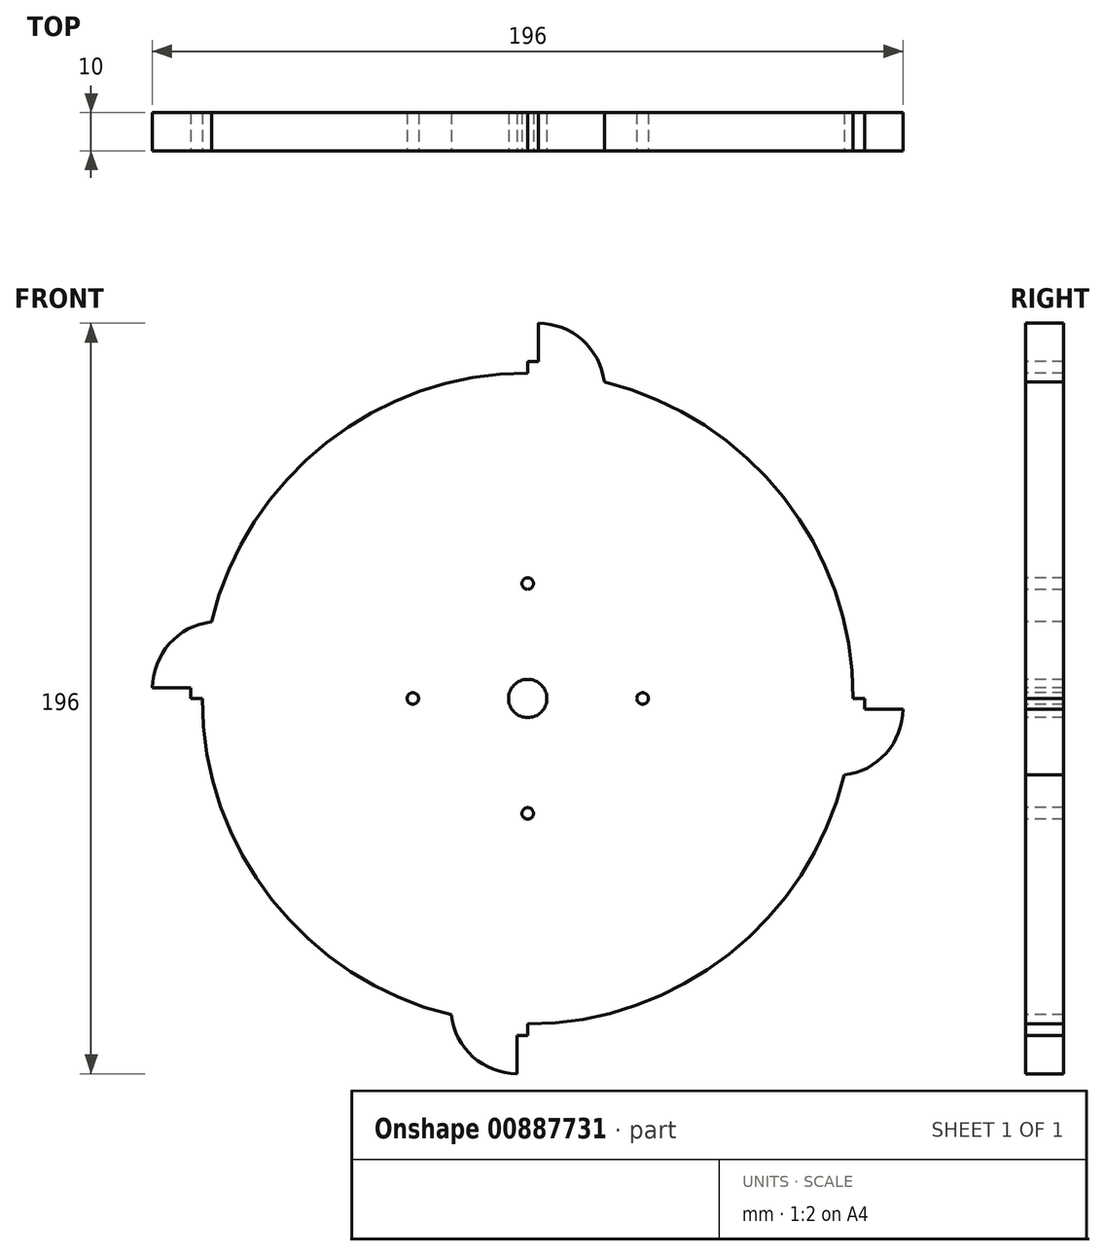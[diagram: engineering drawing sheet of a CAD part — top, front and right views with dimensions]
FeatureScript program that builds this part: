
annotation { "Feature Type Name" : "Feature", "Feature Type Description" : "" }
export const myFeature = defineFeature(function(context is Context, id is Id, definition is map)
    precondition{}
    {
        {
            var Q0;
            Q0=qCreatedBy(makeId("Front.planeOp"),FACE);
            var sketch = newSketch(context, id + "F0", { "sketchPlane" : qUnion([Q0])});
            skCircle(sketch, "E0", {"center": v(0, 0) * mm, "radius": 85 * mm});
            skSolve(sketch);
        }
        {
            var Q0;
            Q0=makeQuery(id+"F0.imprint","IMPRINT",FACE,{"disambiguationData":[TD([[makeQuery(id+"F0.imprint","IMPRINT",EDGE,{"derivedFrom":sQuery(id+"F0.wireOp",EDGE,"E0")}),1.0]])]});
            extrude(context, id + "F1", {"entities" : qUnion([Q0]), "depth" : 10 * mm, "offsetDistance" : 25 * mm});
        }
        {
            var Q0;
            Q0=makeQuery(id+"F1.opExtrude","CAP_FACE",FACE,{"disambiguationData":[OSD([sQuery(id+"F0.wireOp",EDGE,"E0")])],"isStart":false});
            var sketch = newSketch(context, id + "F2", { "sketchPlane" : qUnion([Q0])});
            skLineSegment(sketch, "E1", {"start": v(0, 0) * mm, "end": v(0, 85) * mm});
            skLineSegment(sketch, "E2", {"start": v(0, 85) * mm, "end": v(0, 88) * mm});
            skLineSegment(sketch, "E3", {"start": v(0, 88) * mm, "end": v(2.75, 88) * mm});
            skLineSegment(sketch, "E4", {"start": v(2.75, 88) * mm, "end": v(2.75, 98) * mm});
            skArc(sketch, "E5", {"start": v(20, 82.61) * mm, "mid": v(14.3, 93.6) * mm, "end": v(2.75, 98) * mm});
            skArc(sketch, "E6.1.0", {"start": v(82.61, -20) * mm, "mid": v(93.6, -14.3) * mm, "end": v(98, -2.75) * mm});
            skLineSegment(sketch, "E6.1.1", {"start": v(88, -2.75) * mm, "end": v(98, -2.75) * mm});
            skLineSegment(sketch, "E6.1.2", {"start": v(88, 0) * mm, "end": v(88, -2.75) * mm});
            skLineSegment(sketch, "E6.1.3", {"start": v(85, 0) * mm, "end": v(88, 0) * mm});
            skArc(sketch, "E6.2.0", {"start": v(-20, -82.61) * mm, "mid": v(-14.3, -93.6) * mm, "end": v(-2.75, -98) * mm});
            skLineSegment(sketch, "E6.2.1", {"start": v(-2.75, -88) * mm, "end": v(-2.75, -98) * mm});
            skLineSegment(sketch, "E6.2.2", {"start": v(0, -88) * mm, "end": v(-2.75, -88) * mm});
            skLineSegment(sketch, "E6.2.3", {"start": v(0, -85) * mm, "end": v(0, -88) * mm});
            skArc(sketch, "E6.3.0", {"start": v(-82.61, 20) * mm, "mid": v(-93.6, 14.3) * mm, "end": v(-98, 2.75) * mm});
            skLineSegment(sketch, "E6.3.1", {"start": v(-88, 2.75) * mm, "end": v(-98, 2.75) * mm});
            skLineSegment(sketch, "E6.3.2", {"start": v(-88, 0) * mm, "end": v(-88, 2.75) * mm});
            skLineSegment(sketch, "E6.3.3", {"start": v(-85, 0) * mm, "end": v(-88, 0) * mm});
            skPoint(sketch, "E6.center", {"position": v(0, 0) * mm});
            skLineSegment(sketch, "E6.anchor1", {"start": v(0, 0) * mm, "end": v(0, 85) * mm, "construction": true});
            skLineSegment(sketch, "E6.anchor2", {"start": v(0, 0) * mm, "end": v(-85, 0) * mm, "construction": true});
            skSolve(sketch);
        }
        {
            var Q0;
            Q0 = qSketchRegion(id + "F2", true);
            var Q1;
            {var subQ1=sQuery(id+"F2.wireOp",EDGE,"E2");Q1=makeQuery(id+"F2.imprint","IMPRINT",FACE,{"disambiguationData":[TD([[makeQuery(id+"F2.imprint","IMPRINT",EDGE,{"derivedFrom":subQ1}),-1.0]])]});}
            var Q2;
            {var subQ1=sQuery(id+"F2.wireOp",EDGE,"E6.3.0");Q2=makeQuery(id+"F2.imprint","IMPRINT",FACE,{"disambiguationData":[TD([[makeQuery(id+"F2.imprint","IMPRINT",EDGE,{"derivedFrom":subQ1}),1.0]])]});}
            var Q3;
            {var subQ1=sQuery(id+"F2.wireOp",EDGE,"E6.2.0");Q3=makeQuery(id+"F2.imprint","IMPRINT",FACE,{"disambiguationData":[TD([[makeQuery(id+"F2.imprint","IMPRINT",EDGE,{"derivedFrom":subQ1}),1.0]])]});}
            var Q4;
            {var subQ1=sQuery(id+"F2.wireOp",EDGE,"E6.1.0");Q4=makeQuery(id+"F2.imprint","IMPRINT",FACE,{"disambiguationData":[TD([[makeQuery(id+"F2.imprint","IMPRINT",EDGE,{"derivedFrom":subQ1}),1.0]])]});}
            extrude(context, id + "F3", {"entities" : qUnion([Q0, Q1, Q2, Q3, Q4]), "operationType" : NewBodyOperationType.ADD, "oppositeDirection" : true, "depth" : 10 * mm, "offsetDistance" : 25 * mm});
        }
        {
            var Q0;
            {var subQ0=sQuery(id+"F0.wireOp",EDGE,"E0");Q0=makeQuery(id+"F3.boolean.opBoolean","MERGE",FACE,{"derivedFrom":[makeQuery(id+"F1.opExtrude","CAP_FACE",FACE,{"disambiguationData":[OSD([subQ0])],"isStart":false}),makeQuery(id+"F3.opExtrude","CAP_FACE",FACE,{"disambiguationData":[OSD([subQ0,sQuery(id+"F2.wireOp",EDGE,"E2"),sQuery(id+"F2.wireOp",EDGE,"E3"),sQuery(id+"F2.wireOp",EDGE,"E4"),sQuery(id+"F2.wireOp",EDGE,"E5")])],"isStart":true}),makeQuery(id+"F3.opExtrude","CAP_FACE",FACE,{"disambiguationData":[OSD([subQ0,sQuery(id+"F2.wireOp",EDGE,"E6.1.0"),sQuery(id+"F2.wireOp",EDGE,"E6.1.1"),sQuery(id+"F2.wireOp",EDGE,"E6.1.2"),sQuery(id+"F2.wireOp",EDGE,"E6.1.3")])],"isStart":true}),makeQuery(id+"F3.opExtrude","CAP_FACE",FACE,{"disambiguationData":[OSD([subQ0,sQuery(id+"F2.wireOp",EDGE,"E6.2.0"),sQuery(id+"F2.wireOp",EDGE,"E6.2.1"),sQuery(id+"F2.wireOp",EDGE,"E6.2.2"),sQuery(id+"F2.wireOp",EDGE,"E6.2.3")])],"isStart":true}),makeQuery(id+"F3.opExtrude","CAP_FACE",FACE,{"disambiguationData":[OSD([subQ0,sQuery(id+"F2.wireOp",EDGE,"E6.3.0"),sQuery(id+"F2.wireOp",EDGE,"E6.3.1"),sQuery(id+"F2.wireOp",EDGE,"E6.3.2"),sQuery(id+"F2.wireOp",EDGE,"E6.3.3")])],"isStart":true})]});}
            var sketch = newSketch(context, id + "F4", { "sketchPlane" : qUnion([Q0])});
            skCircle(sketch, "E7", {"center": v(0, 0) * mm, "radius": 5 * mm});
            skCircle(sketch, "E8", {"center": v(0, 30) * mm, "radius": 1.5 * mm});
            skCircle(sketch, "E9.4.0", {"center": v(-30, 0) * mm, "radius": 1.5 * mm});
            skCircle(sketch, "E9.8.0", {"center": v(0, -30) * mm, "radius": 1.5 * mm});
            skCircle(sketch, "E9.12.0", {"center": v(30, 0) * mm, "radius": 1.5 * mm});
            skSolve(sketch);
        }
        {
            var Q0;
            Q0=makeQuery(id+"F4.imprint","IMPRINT",FACE,{"disambiguationData":[TD([[makeQuery(id+"F4.imprint","IMPRINT",EDGE,{"derivedFrom":sQuery(id+"F4.wireOp",EDGE,"E7")}),1.0]])]});
            var Q1;
            Q1=makeQuery(id+"F4.imprint","IMPRINT",FACE,{"disambiguationData":[TD([[makeQuery(id+"F4.imprint","IMPRINT",EDGE,{"derivedFrom":sQuery(id+"F4.wireOp",EDGE,"E8")}),1.0]])]});
            var Q2;
            Q2=makeQuery(id+"F4.imprint","IMPRINT",FACE,{"disambiguationData":[TD([[makeQuery(id+"F4.imprint","IMPRINT",EDGE,{"derivedFrom":sQuery(id+"F4.wireOp",EDGE,"E9.15.0")}),1.0]])]});
            var Q3;
            Q3=makeQuery(id+"F4.imprint","IMPRINT",FACE,{"disambiguationData":[TD([[makeQuery(id+"F4.imprint","IMPRINT",EDGE,{"derivedFrom":sQuery(id+"F4.wireOp",EDGE,"E9.14.0")}),1.0]])]});
            var Q4;
            Q4=makeQuery(id+"F4.imprint","IMPRINT",FACE,{"disambiguationData":[TD([[makeQuery(id+"F4.imprint","IMPRINT",EDGE,{"derivedFrom":sQuery(id+"F4.wireOp",EDGE,"E9.13.0")}),1.0]])]});
            var Q5;
            Q5=makeQuery(id+"F4.imprint","IMPRINT",FACE,{"disambiguationData":[TD([[makeQuery(id+"F4.imprint","IMPRINT",EDGE,{"derivedFrom":sQuery(id+"F4.wireOp",EDGE,"E9.12.0")}),1.0]])]});
            var Q6;
            Q6=makeQuery(id+"F4.imprint","IMPRINT",FACE,{"disambiguationData":[TD([[makeQuery(id+"F4.imprint","IMPRINT",EDGE,{"derivedFrom":sQuery(id+"F4.wireOp",EDGE,"E9.1.0")}),1.0]])]});
            var Q7;
            Q7=makeQuery(id+"F4.imprint","IMPRINT",FACE,{"disambiguationData":[TD([[makeQuery(id+"F4.imprint","IMPRINT",EDGE,{"derivedFrom":sQuery(id+"F4.wireOp",EDGE,"E9.2.0")}),1.0]])]});
            var Q8;
            Q8=makeQuery(id+"F4.imprint","IMPRINT",FACE,{"disambiguationData":[TD([[makeQuery(id+"F4.imprint","IMPRINT",EDGE,{"derivedFrom":sQuery(id+"F4.wireOp",EDGE,"E9.3.0")}),1.0]])]});
            var Q9;
            Q9=makeQuery(id+"F4.imprint","IMPRINT",FACE,{"disambiguationData":[TD([[makeQuery(id+"F4.imprint","IMPRINT",EDGE,{"derivedFrom":sQuery(id+"F4.wireOp",EDGE,"E9.4.0")}),1.0]])]});
            var Q10;
            Q10=makeQuery(id+"F4.imprint","IMPRINT",FACE,{"disambiguationData":[TD([[makeQuery(id+"F4.imprint","IMPRINT",EDGE,{"derivedFrom":sQuery(id+"F4.wireOp",EDGE,"E9.5.0")}),1.0]])]});
            var Q11;
            Q11=makeQuery(id+"F4.imprint","IMPRINT",FACE,{"disambiguationData":[TD([[makeQuery(id+"F4.imprint","IMPRINT",EDGE,{"derivedFrom":sQuery(id+"F4.wireOp",EDGE,"E9.6.0")}),1.0]])]});
            var Q12;
            Q12=makeQuery(id+"F4.imprint","IMPRINT",FACE,{"disambiguationData":[TD([[makeQuery(id+"F4.imprint","IMPRINT",EDGE,{"derivedFrom":sQuery(id+"F4.wireOp",EDGE,"E9.7.0")}),1.0]])]});
            var Q13;
            Q13=makeQuery(id+"F4.imprint","IMPRINT",FACE,{"disambiguationData":[TD([[makeQuery(id+"F4.imprint","IMPRINT",EDGE,{"derivedFrom":sQuery(id+"F4.wireOp",EDGE,"E9.8.0")}),1.0]])]});
            var Q14;
            Q14=makeQuery(id+"F4.imprint","IMPRINT",FACE,{"disambiguationData":[TD([[makeQuery(id+"F4.imprint","IMPRINT",EDGE,{"derivedFrom":sQuery(id+"F4.wireOp",EDGE,"E9.9.0")}),1.0]])]});
            var Q15;
            Q15=makeQuery(id+"F4.imprint","IMPRINT",FACE,{"disambiguationData":[TD([[makeQuery(id+"F4.imprint","IMPRINT",EDGE,{"derivedFrom":sQuery(id+"F4.wireOp",EDGE,"E9.10.0")}),1.0]])]});
            var Q16;
            Q16=makeQuery(id+"F4.imprint","IMPRINT",FACE,{"disambiguationData":[TD([[makeQuery(id+"F4.imprint","IMPRINT",EDGE,{"derivedFrom":sQuery(id+"F4.wireOp",EDGE,"E9.11.0")}),1.0]])]});
            extrude(context, id + "F5", {"entities" : qUnion([Q0, Q1, Q2, Q3, Q4, Q5, Q6, Q7, Q8, Q9, Q10, Q11, Q12, Q13, Q14, Q15, Q16]), "operationType" : NewBodyOperationType.REMOVE, "endBound" : BoundingType.THROUGH_ALL, "oppositeDirection" : true, "depth" : 25 * mm, "offsetDistance" : 25 * mm});
        }
    });
